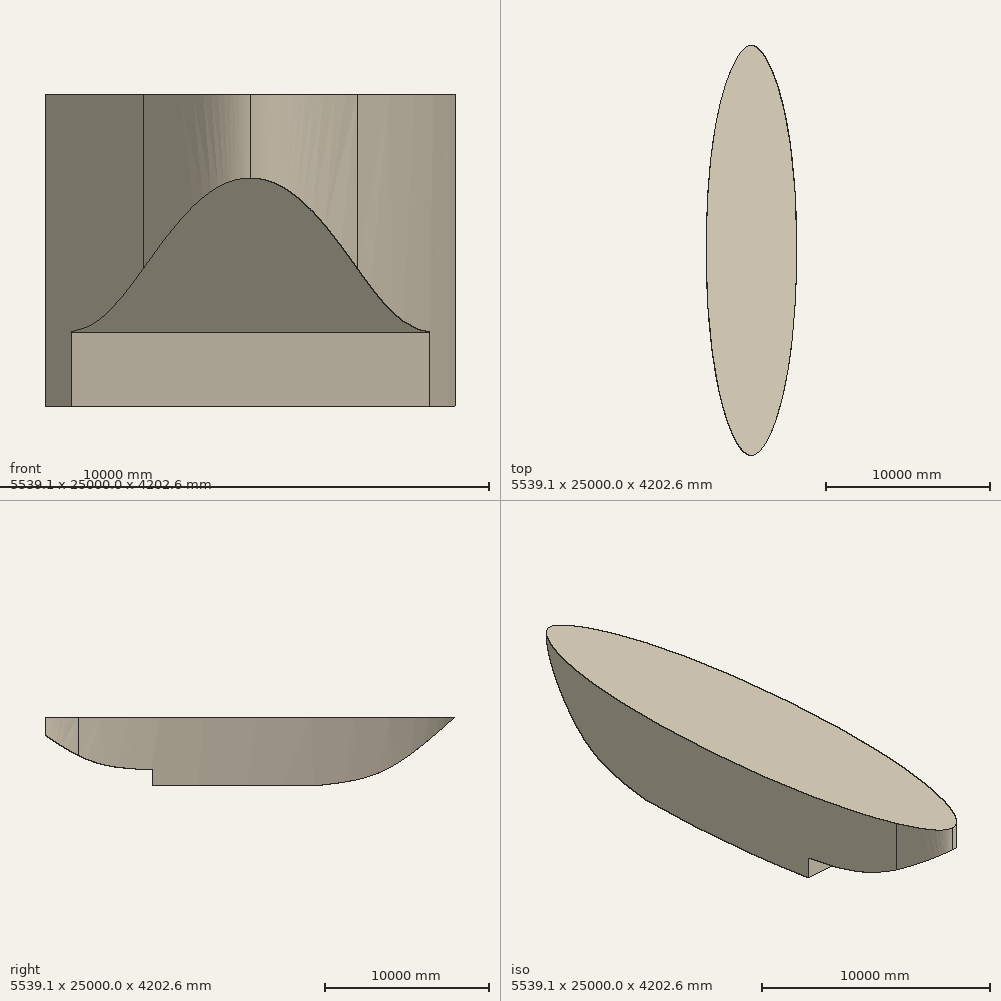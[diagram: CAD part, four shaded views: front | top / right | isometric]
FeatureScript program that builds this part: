
annotation { "Feature Type Name" : "Feature", "Feature Type Description" : "" }
export const myFeature = defineFeature(function(context is Context, id is Id, definition is map)
    precondition{}
    {
        {
            var Q0;
            Q0=qCreatedBy(makeId("Top.planeOp"),FACE);
            var sketch = newSketch(context, id + "F0", { "sketchPlane" : qUnion([Q0])});
            skCircle(sketch, "E0", {"center": v(0, 8280.46) * mm, "radius": 2500 * mm, "construction": true});
            skCircle(sketch, "E1", {"center": v(0, -5719.54) * mm, "radius": 2000 * mm, "construction": true});
            skCircle(sketch, "E2", {"center": v(0, 14280.46) * mm, "radius": 1000 * mm, "construction": true});
            skLineSegment(sketch, "E3", {"start": v(0, -5719.54) * mm, "end": v(2000, -5719.54) * mm, "construction": true});
            skLineSegment(sketch, "E4", {"start": v(2498.9, 8206.06) * mm, "end": v(-2498.9, 8206.06) * mm, "construction": true});
            skLineSegment(sketch, "E5", {"start": v(0, -5719.54) * mm, "end": v(-2000, -5719.54) * mm, "construction": true});
            skLineSegment(sketch, "E6", {"start": v(0, 14280.46) * mm, "end": v(0, -5719.54) * mm, "construction": true});
            skLineSegment(sketch, "E7", {"start": v(0, -9719.54) * mm, "end": v(0, -5719.54) * mm, "construction": true});
            skLineSegment(sketch, "E8", {"start": v(0, 14280.46) * mm, "end": v(0, 15280.46) * mm, "construction": true});
            skLineSegment(sketch, "E9", {"start": v(0, 14280.46) * mm, "end": v(-1000, 14280.46) * mm, "construction": true});
            skLineSegment(sketch, "E10", {"start": v(-1000, 14280.46) * mm, "end": v(1000, 14280.46) * mm, "construction": true});
            skFitSpline(sketch, "E11", {"points": [v(0, 15280.46) * mm, v(-1000, 14280.46) * mm, v(-2498.9, 8206.06) * mm, v(-2000, -5719.54) * mm, v(0, -9719.54) * mm, v(2000, -5719.54) * mm, v(2498.9, 8206.06) * mm, v(1000, 14280.46) * mm, v(0, 15280.46) * mm]});
            skLineSegment(sketch, "E12", {"start": v(-1446.21, -7719.54) * mm, "end": v(1446.21, -7719.54) * mm});
            skLineSegment(sketch, "E13.bottom", {"start": v(-3500, -9719.54) * mm, "end": v(3500, -9719.54) * mm});
            skLineSegment(sketch, "E13.top", {"start": v(-3500, 15280.46) * mm, "end": v(3500, 15280.46) * mm});
            skLineSegment(sketch, "E13.left", {"start": v(-3500, -9719.54) * mm, "end": v(-3500, 15280.46) * mm});
            skLineSegment(sketch, "E13.right", {"start": v(3500, -9719.54) * mm, "end": v(3500, 15280.46) * mm});
            skSolve(sketch);
        }
        {
            var Q0;
            {var subQ0=sQuery(id+"F0.wireOp",EDGE,"E13.right");Q0=makeQuery(id+"F0.imprint","IMPRINT",FACE,{"disambiguationData":[TD([[makeQuery(id+"F0.imprint","IMPRINT",EDGE,{"derivedFrom":subQ0}),1.0]])]});}
            var Q1;
            {var subQ0=sQuery(id+"F0.wireOp",EDGE,"E13.left");Q1=makeQuery(id+"F0.imprint","IMPRINT",FACE,{"disambiguationData":[TD([[makeQuery(id+"F0.imprint","IMPRINT",EDGE,{"derivedFrom":subQ0}),-1.0]])]});}
            var Q2;
            {var subQ0=sQuery(id+"F0.wireOp",EDGE,"E12");Q2=makeQuery(id+"F0.imprint","IMPRINT",FACE,{"disambiguationData":[TD([[makeQuery(id+"F0.imprint","IMPRINT",EDGE,{"derivedFrom":subQ0}),1.0]])]});}
            var Q3;
            {var subQ0=sQuery(id+"F0.wireOp",EDGE,"E12");Q3=makeQuery(id+"F0.imprint","IMPRINT",FACE,{"disambiguationData":[TD([[makeQuery(id+"F0.imprint","IMPRINT",EDGE,{"derivedFrom":subQ0}),-1.0]])]});}
            var Q4;
            Q4=sQuery(id+"F0.wireOp",EDGE,"E2");
            var Q5;
            Q5=sQuery(id+"F0.wireOp",EDGE,"E0");
            var Q6;
            Q6=sQuery(id+"F0.wireOp",EDGE,"E1");
            var Q7;
            Q7=sQuery(id+"F0.wireOp",EDGE,"E11");
            extrude(context, id + "F1", {"entities" : qUnion([Q0, Q1, Q2, Q3]), "surfaceEntities" : qUnion([Q4, Q5, Q6, Q7]), "depth" : -5000 * mm, "offsetDistance" : 25 * mm});
        }
        {
            var Q0;
            Q0=makeQuery(id+"F1.opExtrude","SWEPT_FACE",FACE,{"disambiguationData":[OSD([sQuery(id+"F0.wireOp",EDGE,"E13.left")])]});
            var sketch = newSketch(context, id + "F2", { "sketchPlane" : qUnion([Q0])});
            skFitSpline(sketch, "E14", {"points": [v(-15280.46, 0) * mm, v(-10782.58, -3343.12) * mm, v(-6708.78, -4202.65) * mm], "startDerivative": vector(8272.5, -7360.86) * mm, "endDerivative": vector(8885.84, -1039.58) * mm});
            skLineSegment(sketch, "E15", {"start": v(-6708.78, -4202.65) * mm, "end": v(3203.92, -4202.65) * mm});
            skLineSegment(sketch, "E16", {"start": v(3203.92, -4202.65) * mm, "end": v(3203.92, -3202.65) * mm});
            skFitSpline(sketch, "E17", {"points": [v(3203.92, -3202.65) * mm, v(7668.06, -2376.51) * mm, v(9719.54, -1126.76) * mm, v(9719.54, -1130.19) * mm, v(9719.54, -1140.85) * mm], "startDerivative": vector(9750.93, 157.96) * mm, "endDerivative": vector(41.85, -451.34) * mm});
            skSolve(sketch);
        }
        {
            var Q0;
            {var subQ0=sQuery(id+"F0.wireOp",EDGE,"E13.left");Q0=makeQuery(id+"F0.imprint","IMPRINT",FACE,{"disambiguationData":[TD([[makeQuery(id+"F0.imprint","IMPRINT",EDGE,{"derivedFrom":subQ0}),-1.0]])]});}
            var Q1;
            {var subQ0=sQuery(id+"F0.wireOp",EDGE,"E13.right");Q1=makeQuery(id+"F0.imprint","IMPRINT",FACE,{"disambiguationData":[TD([[makeQuery(id+"F0.imprint","IMPRINT",EDGE,{"derivedFrom":subQ0}),1.0]])]});}
            extrude(context, id + "F3", {"entities" : qUnion([Q0, Q1]), "operationType" : NewBodyOperationType.REMOVE, "endBound" : BoundingType.THROUGH_ALL, "oppositeDirection" : true, "depth" : 25 * mm, "offsetDistance" : 25 * mm});
        }
        {
            var Q0;
            Q0=makeQuery(id+"F2.imprint","IMPRINT",FACE,{"disambiguationData":[TD([[makeQuery(id+"F2.imprint","IMPRINT",EDGE,{"derivedFrom":sQuery(id+"F2.wireOp",EDGE,"E14")}),1.0]])]});
            extrude(context, id + "F4", {"entities" : qUnion([Q0]), "operationType" : NewBodyOperationType.INTERSECT, "depth" : -10000 * mm, "offsetDistance" : 25 * mm});
        }
    });
